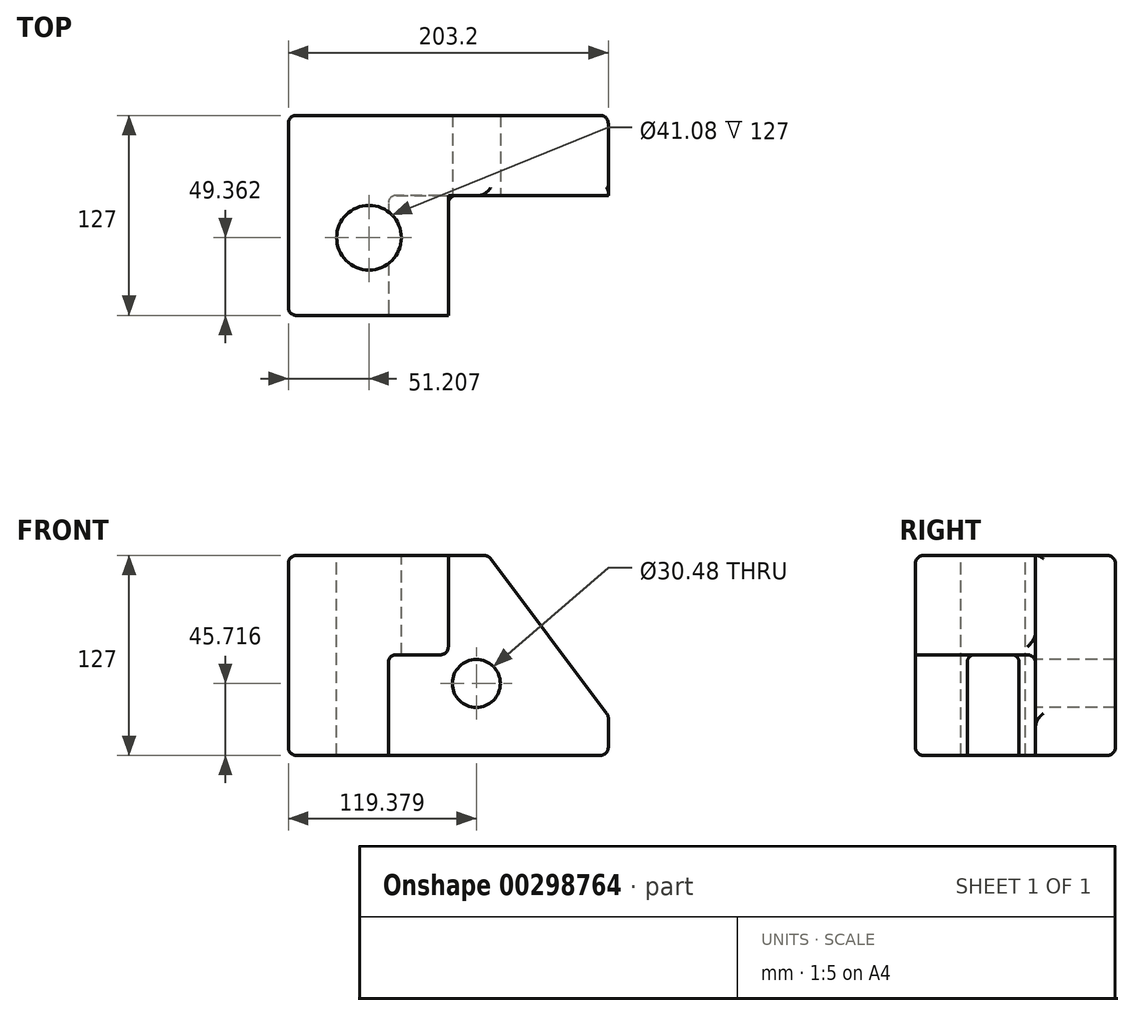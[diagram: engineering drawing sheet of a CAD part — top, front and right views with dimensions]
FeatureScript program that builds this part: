
annotation { "Feature Type Name" : "Feature", "Feature Type Description" : "" }
export const myFeature = defineFeature(function(context is Context, id is Id, definition is map)
    precondition{}
    {
        {
            var Q0;
            Q0=qCreatedBy(makeId("Front.planeOp"),FACE);
            var sketch = newSketch(context, id + "F0", { "sketchPlane" : qUnion([Q0])});
            skLineSegment(sketch, "E0.bottom", {"start": v(-98.65, 63.04) * mm, "end": v(104.55, 63.04) * mm});
            skLineSegment(sketch, "E0.top", {"start": v(-98.65, -63.96) * mm, "end": v(104.55, -63.96) * mm});
            skLineSegment(sketch, "E0.left", {"start": v(-98.65, 63.04) * mm, "end": v(-98.65, -63.96) * mm});
            skLineSegment(sketch, "E0.right", {"start": v(104.55, 63.04) * mm, "end": v(104.55, -63.96) * mm});
            skSolve(sketch);
        }
        {
            var Q0;
            Q0=makeQuery(id+"F0.imprint","IMPRINT",FACE,{"disambiguationData":[TD([[makeQuery(id+"F0.imprint","IMPRINT",EDGE,{"derivedFrom":sQuery(id+"F0.wireOp",EDGE,"E0.bottom")}),-1.0]])]});
            extrude(context, id + "F1", {"entities" : qUnion([Q0]), "depth" : 127 * mm});
        }
        {
            var Q0;
            Q0=makeQuery(id+"F1.opExtrude","CAP_FACE",FACE,{"disambiguationData":[OSD([sQuery(id+"F0.wireOp",EDGE,"E0.bottom"),sQuery(id+"F0.wireOp",EDGE,"E0.top"),sQuery(id+"F0.wireOp",EDGE,"E0.left"),sQuery(id+"F0.wireOp",EDGE,"E0.right")])],"isStart":false});
            var sketch = newSketch(context, id + "F2", { "sketchPlane" : qUnion([Q0])});
            skLineSegment(sketch, "E1", {"start": v(-98.65, -63.96) * mm, "end": v(-98.65, 63.04) * mm});
            skLineSegment(sketch, "E2", {"start": v(-98.65, 63.04) * mm, "end": v(2.95, 63.04) * mm});
            skLineSegment(sketch, "E3", {"start": v(2.95, 63.04) * mm, "end": v(2.95, 0) * mm});
            skLineSegment(sketch, "E4", {"start": v(2.95, 0) * mm, "end": v(-35.15, 0) * mm});
            skLineSegment(sketch, "E5", {"start": v(-35.15, 0) * mm, "end": v(-35.15, -63.96) * mm});
            skLineSegment(sketch, "E6", {"start": v(-35.15, -63.96) * mm, "end": v(-98.65, -63.96) * mm});
            skSolve(sketch);
        }
        {
            var Q0;
            {var subQ2=sQuery(id+"F2.wireOp",EDGE,"E3");Q0=makeQuery(id+"F2.imprint","IMPRINT",FACE,{"disambiguationData":[TD([[makeQuery(id+"F2.imprint","IMPRINT",EDGE,{"derivedFrom":subQ2}),1.0]])]});}
            extrude(context, id + "F3", {"entities" : qUnion([Q0]), "operationType" : NewBodyOperationType.REMOVE, "oppositeDirection" : true, "depth" : 76.2 * mm});
        }
        {
            var Q0;
            Q0=makeQuery(id+"F1.opExtrude","SWEPT_EDGE",EDGE,{"disambiguationData":[OSD([sQuery(id+"F0.wireOp",EDGE,"E0.bottom"),sQuery(id+"F0.wireOp",EDGE,"E0.right")])]});
            chamfer(context, id + "F4", {"entities" : qUnion([Q0]), "chamferType" : ChamferType.TWO_OFFSETS, "width1" : 76.2 * mm, "oppositeDirection" : false, "width2" : 101.6 * mm, "tangentPropagation" : true});
        }
        {
            var Q0;
            Q0=makeQuery(id+"F1.opExtrude","SWEPT_EDGE",EDGE,{"disambiguationData":[OSD([sQuery(id+"F0.wireOp",EDGE,"E0.bottom"),sQuery(id+"F0.wireOp",EDGE,"E0.left")])]});
            var Q1;
            Q1=makeQuery(id+"F1.opExtrude","CAP_EDGE",EDGE,{"disambiguationData":[OSD([sQuery(id+"F0.wireOp",EDGE,"E0.bottom")])],"isStart":false});
            var Q2;
            Q2=makeQuery(id+"F3.boolean.opBoolean","COPY",EDGE,{"derivedFrom":makeQuery(id+"F3.opExtrude","SWEPT_EDGE",EDGE,{"disambiguationData":[OSD([sQuery(id+"F0.wireOp",EDGE,"E0.bottom"),sQuery(id+"F2.wireOp",EDGE,"E2"),sQuery(id+"F2.wireOp",EDGE,"E3")])]})});
            var Q3;
            Q3=makeQuery(id+"F3.boolean.opBoolean","COPY",EDGE,{"derivedFrom":makeQuery(id+"F3.opExtrude","CAP_EDGE",EDGE,{"disambiguationData":[OSD([sQuery(id+"F0.wireOp",EDGE,"E0.bottom")])],"isStart":false})});
            var Q4;
            {var subQ0=sQuery(id+"F0.wireOp",EDGE,"E0.bottom");Q4=makeQuery(id+"F4.opChamfer","BLEND_EDGE",EDGE,{"blendedFrom":[makeQuery(id+"F1.opExtrude","SWEPT_EDGE",EDGE,{"disambiguationData":[OSD([subQ0,sQuery(id+"F0.wireOp",EDGE,"E0.right")])]}),makeQuery(id+"F1.opExtrude","SWEPT_FACE",FACE,{"disambiguationData":[OSD([subQ0])]})],"blendedInto":[makeQuery(id+"F1.opExtrude","SWEPT_FACE",FACE,{"disambiguationData":[OSD([subQ0])]})]});}
            var Q5;
            Q5=makeQuery(id+"F1.opExtrude","CAP_EDGE",EDGE,{"disambiguationData":[OSD([sQuery(id+"F0.wireOp",EDGE,"E0.bottom")])],"isStart":true});
            var Q6;
            Q6=makeQuery(id+"F3.boolean.opBoolean","COPY",EDGE,{"derivedFrom":makeQuery(id+"F3.opExtrude","CAP_EDGE",EDGE,{"disambiguationData":[OSD([sQuery(id+"F2.wireOp",EDGE,"E3")])],"isStart":true})});
            var Q7;
            Q7=makeQuery(id+"F3.boolean.opBoolean","COPY",EDGE,{"derivedFrom":makeQuery(id+"F3.opExtrude","SWEPT_EDGE",EDGE,{"disambiguationData":[OSD([sQuery(id+"F2.wireOp",EDGE,"E3"),sQuery(id+"F2.wireOp",EDGE,"E4")])]})});
            var Q8;
            Q8=makeQuery(id+"F3.boolean.opBoolean","COPY",EDGE,{"derivedFrom":makeQuery(id+"F3.opExtrude","CAP_EDGE",EDGE,{"disambiguationData":[OSD([sQuery(id+"F2.wireOp",EDGE,"E5")])],"isStart":true})});
            var Q9;
            Q9=makeQuery(id+"F3.boolean.opBoolean","COPY",EDGE,{"derivedFrom":makeQuery(id+"F3.opExtrude","CAP_EDGE",EDGE,{"disambiguationData":[OSD([sQuery(id+"F2.wireOp",EDGE,"E4")])],"isStart":true})});
            var Q10;
            Q10=makeQuery(id+"F3.boolean.opBoolean","COPY",EDGE,{"derivedFrom":makeQuery(id+"F3.opExtrude","CAP_EDGE",EDGE,{"disambiguationData":[OSD([sQuery(id+"F2.wireOp",EDGE,"E4")])],"isStart":false})});
            var Q11;
            Q11=makeQuery(id+"F3.boolean.opBoolean","COPY",EDGE,{"derivedFrom":makeQuery(id+"F3.opExtrude","SWEPT_EDGE",EDGE,{"disambiguationData":[OSD([sQuery(id+"F2.wireOp",EDGE,"E4"),sQuery(id+"F2.wireOp",EDGE,"E5")])]})});
            var Q12;
            Q12=makeQuery(id+"F3.boolean.opBoolean","COPY",EDGE,{"derivedFrom":makeQuery(id+"F3.opExtrude","CAP_EDGE",EDGE,{"disambiguationData":[OSD([sQuery(id+"F2.wireOp",EDGE,"E5")])],"isStart":false})});
            var Q13;
            Q13=makeQuery(id+"F1.opExtrude","CAP_EDGE",EDGE,{"disambiguationData":[OSD([sQuery(id+"F0.wireOp",EDGE,"E0.top")])],"isStart":false});
            var Q14;
            Q14=makeQuery(id+"F3.boolean.opBoolean","COPY",EDGE,{"derivedFrom":makeQuery(id+"F3.opExtrude","SWEPT_EDGE",EDGE,{"disambiguationData":[OSD([sQuery(id+"F0.wireOp",EDGE,"E0.top"),sQuery(id+"F2.wireOp",EDGE,"E5"),sQuery(id+"F2.wireOp",EDGE,"E6")])]})});
            var Q15;
            Q15=makeQuery(id+"F3.boolean.opBoolean","COPY",EDGE,{"derivedFrom":makeQuery(id+"F3.opExtrude","CAP_EDGE",EDGE,{"disambiguationData":[OSD([sQuery(id+"F0.wireOp",EDGE,"E0.top")])],"isStart":false})});
            var Q16;
            Q16=makeQuery(id+"F1.opExtrude","SWEPT_EDGE",EDGE,{"disambiguationData":[OSD([sQuery(id+"F0.wireOp",EDGE,"E0.top"),sQuery(id+"F0.wireOp",EDGE,"E0.right")])]});
            var Q17;
            Q17=makeQuery(id+"F3.boolean.opBoolean","COPY",EDGE,{"derivedFrom":makeQuery(id+"F3.opExtrude","CAP_EDGE",EDGE,{"disambiguationData":[OSD([sQuery(id+"F0.wireOp",EDGE,"E0.right")])],"isStart":false})});
            var Q18;
            Q18=makeQuery(id+"F1.opExtrude","CAP_EDGE",EDGE,{"disambiguationData":[OSD([sQuery(id+"F0.wireOp",EDGE,"E0.right")])],"isStart":true});
            var Q19;
            {var subQ0=sQuery(id+"F0.wireOp",EDGE,"E0.right");Q19=makeQuery(id+"F4.opChamfer","BLEND_EDGE",EDGE,{"blendedFrom":[makeQuery(id+"F1.opExtrude","SWEPT_EDGE",EDGE,{"disambiguationData":[OSD([sQuery(id+"F0.wireOp",EDGE,"E0.bottom"),subQ0])]}),makeQuery(id+"F1.opExtrude","SWEPT_FACE",FACE,{"disambiguationData":[OSD([subQ0])]})],"blendedInto":[makeQuery(id+"F1.opExtrude","SWEPT_FACE",FACE,{"disambiguationData":[OSD([subQ0])]})]});}
            var Q20;
            {var subQ0=sQuery(id+"F0.wireOp",EDGE,"E0.right");var subQ1=sQuery(id+"F0.wireOp",EDGE,"E0.bottom");Q20=makeQuery(id+"F4.opChamfer","BLEND_EDGE",EDGE,{"blendedFrom":[makeQuery(id+"F1.opExtrude","SWEPT_EDGE",EDGE,{"disambiguationData":[OSD([subQ1,subQ0])]}),makeQuery(id+"F1.opExtrude","CAP_FACE",FACE,{"disambiguationData":[OSD([subQ1,sQuery(id+"F0.wireOp",EDGE,"E0.top"),sQuery(id+"F0.wireOp",EDGE,"E0.left"),subQ0])],"isStart":true})],"blendedInto":[makeQuery(id+"F1.opExtrude","CAP_FACE",FACE,{"disambiguationData":[OSD([subQ1,sQuery(id+"F0.wireOp",EDGE,"E0.top"),sQuery(id+"F0.wireOp",EDGE,"E0.left"),subQ0])],"isStart":true})]});}
            var Q21;
            {var subQ0=sQuery(id+"F0.wireOp",EDGE,"E0.right");var subQ1=sQuery(id+"F0.wireOp",EDGE,"E0.bottom");Q21=makeQuery(id+"F4.opChamfer","BLEND_EDGE",EDGE,{"blendedFrom":[makeQuery(id+"F1.opExtrude","SWEPT_EDGE",EDGE,{"disambiguationData":[OSD([subQ1,subQ0])]}),makeQuery(id+"F3.boolean.opBoolean","COPY",FACE,{"derivedFrom":makeQuery(id+"F3.opExtrude","CAP_FACE",FACE,{"disambiguationData":[OSD([subQ1,sQuery(id+"F0.wireOp",EDGE,"E0.top"),subQ0,sQuery(id+"F2.wireOp",EDGE,"E3"),sQuery(id+"F2.wireOp",EDGE,"E4"),sQuery(id+"F2.wireOp",EDGE,"E5")])],"isStart":false})})],"blendedInto":[makeQuery(id+"F3.boolean.opBoolean","COPY",FACE,{"derivedFrom":makeQuery(id+"F3.opExtrude","CAP_FACE",FACE,{"disambiguationData":[OSD([subQ1,sQuery(id+"F0.wireOp",EDGE,"E0.top"),subQ0,sQuery(id+"F2.wireOp",EDGE,"E3"),sQuery(id+"F2.wireOp",EDGE,"E4"),sQuery(id+"F2.wireOp",EDGE,"E5")])],"isStart":false})})]});}
            var Q22;
            Q22=makeQuery(id+"F1.opExtrude","CAP_EDGE",EDGE,{"disambiguationData":[OSD([sQuery(id+"F0.wireOp",EDGE,"E0.left")])],"isStart":true});
            var Q23;
            Q23=makeQuery(id+"F1.opExtrude","CAP_EDGE",EDGE,{"disambiguationData":[OSD([sQuery(id+"F0.wireOp",EDGE,"E0.top")])],"isStart":true});
            var Q24;
            Q24=makeQuery(id+"F1.opExtrude","SWEPT_EDGE",EDGE,{"disambiguationData":[OSD([sQuery(id+"F0.wireOp",EDGE,"E0.top"),sQuery(id+"F0.wireOp",EDGE,"E0.left")])]});
            var Q25;
            Q25=makeQuery(id+"F1.opExtrude","SWEPT_FACE",FACE,{"disambiguationData":[OSD([sQuery(id+"F0.wireOp",EDGE,"E0.left")])]});
            fillet(context, id + "F5", {"entities" : qUnion([Q0, Q1, Q2, Q3, Q4, Q5, Q6, Q7, Q8, Q9, Q10, Q11, Q12, Q13, Q14, Q15, Q16, Q17, Q18, Q19, Q20, Q21, Q22, Q23, Q24, Q25]), "radius" : 5.08 * mm, "tangentPropagation" : true, "allowEdgeOverflow" : false});
        }
        {
            var Q0;
            Q0=makeQuery(id+"F3.boolean.opBoolean","COPY",FACE,{"derivedFrom":makeQuery(id+"F3.opExtrude","CAP_FACE",FACE,{"disambiguationData":[OSD([sQuery(id+"F0.wireOp",EDGE,"E0.bottom"),sQuery(id+"F0.wireOp",EDGE,"E0.top"),sQuery(id+"F0.wireOp",EDGE,"E0.right"),sQuery(id+"F2.wireOp",EDGE,"E3"),sQuery(id+"F2.wireOp",EDGE,"E4"),sQuery(id+"F2.wireOp",EDGE,"E5")])],"isStart":false})});
            var sketch = newSketch(context, id + "F6", { "sketchPlane" : qUnion([Q0])});
            skCircle(sketch, "E7", {"center": v(20.73, -18.24) * mm, "radius": 15.24 * mm});
            skSolve(sketch);
        }
        {
            var Q0;
            Q0=makeQuery(id+"F6.imprint","IMPRINT",FACE,{"disambiguationData":[TD([[makeQuery(id+"F6.imprint","IMPRINT",EDGE,{"derivedFrom":sQuery(id+"F6.wireOp",EDGE,"E7")}),1.0]])]});
            var Q1;
            Q1=makeQuery(id+"F1.opExtrude","CAP_FACE",FACE,{"disambiguationData":[OSD([sQuery(id+"F0.wireOp",EDGE,"E0.bottom"),sQuery(id+"F0.wireOp",EDGE,"E0.top"),sQuery(id+"F0.wireOp",EDGE,"E0.left"),sQuery(id+"F0.wireOp",EDGE,"E0.right")])],"isStart":true});
            extrude(context, id + "F7", {"entities" : qUnion([Q0]), "operationType" : NewBodyOperationType.REMOVE, "endBound" : BoundingType.UP_TO_SURFACE, "oppositeDirection" : true, "endBoundEntityFace" : qUnion([Q1]), "depth" : 25.4 * mm});
        }
        {
            var Q0;
            Q0=makeQuery(id+"F1.opExtrude","SWEPT_FACE",FACE,{"disambiguationData":[OSD([sQuery(id+"F0.wireOp",EDGE,"E0.bottom")])]});
            var sketch = newSketch(context, id + "F8", { "sketchPlane" : qUnion([Q0])});
            skCircle(sketch, "E8", {"center": v(-47.44, -77.64) * mm, "radius": 20.54 * mm});
            skSolve(sketch);
        }
        {
            var Q0;
            Q0=makeQuery(id+"F8.imprint","IMPRINT",FACE,{"disambiguationData":[TD([[makeQuery(id+"F8.imprint","IMPRINT",EDGE,{"derivedFrom":sQuery(id+"F8.wireOp",EDGE,"E8")}),1.0]])]});
            var Q1;
            Q1=makeQuery(id+"F1.opExtrude","SWEPT_FACE",FACE,{"disambiguationData":[OSD([sQuery(id+"F0.wireOp",EDGE,"E0.top")])]});
            extrude(context, id + "F9", {"entities" : qUnion([Q0]), "operationType" : NewBodyOperationType.REMOVE, "endBound" : BoundingType.UP_TO_SURFACE, "oppositeDirection" : true, "endBoundEntityFace" : qUnion([Q1]), "depth" : 25.4 * mm});
        }
    });
